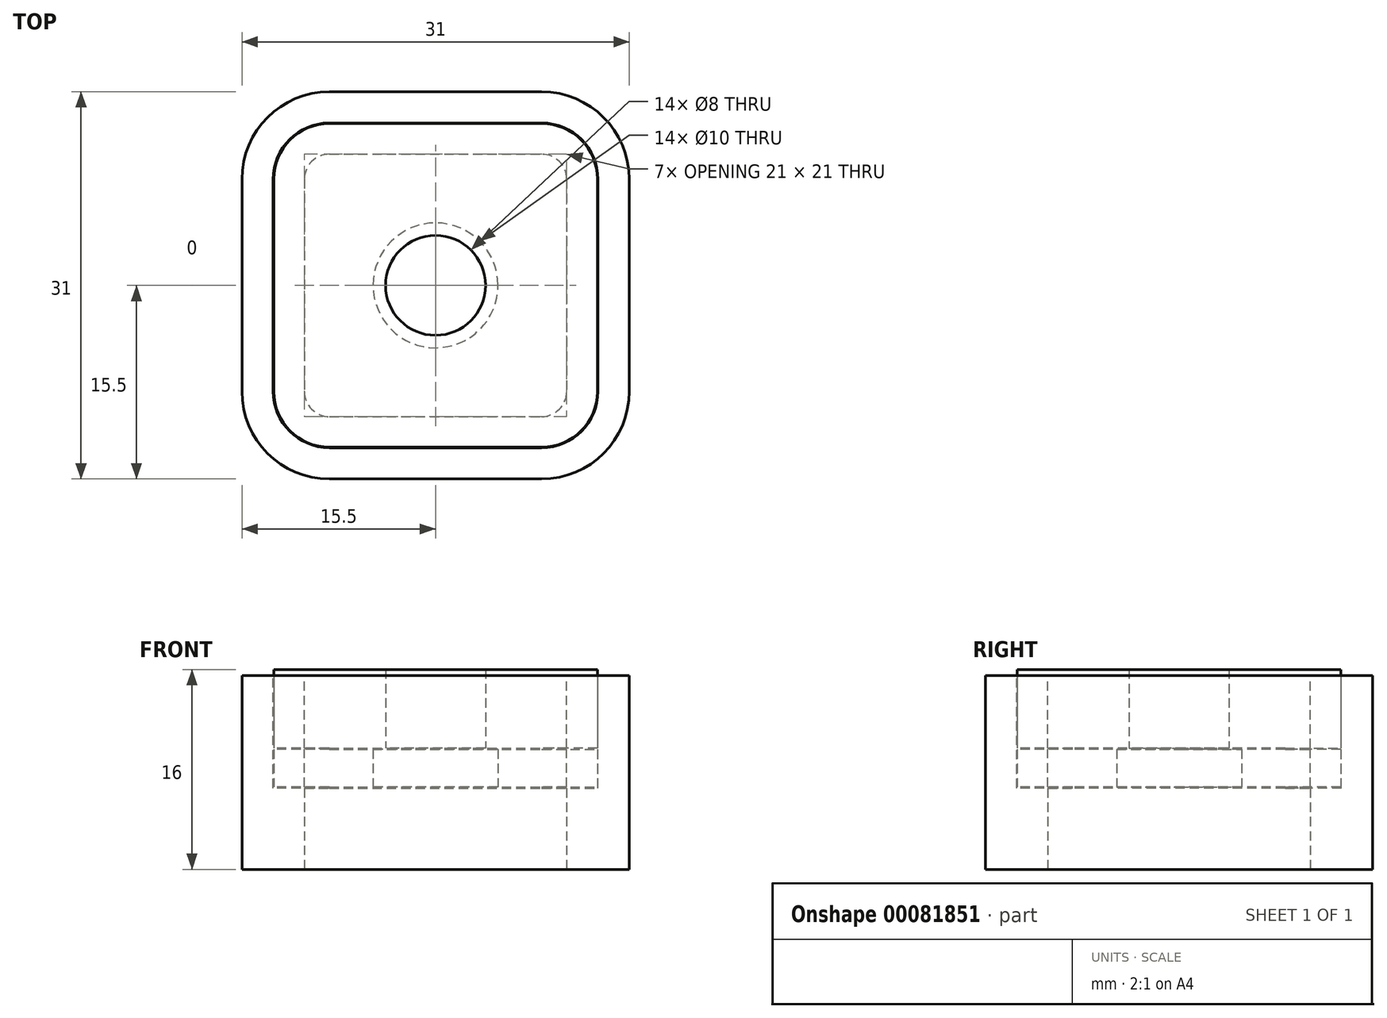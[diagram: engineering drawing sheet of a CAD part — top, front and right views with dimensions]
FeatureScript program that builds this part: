
annotation { "Feature Type Name" : "Feature", "Feature Type Description" : "" }
export const myFeature = defineFeature(function(context is Context, id is Id, definition is map)
    precondition{}
    {
        {
            var Q0;
            Q0=qCreatedBy(makeId("Top.planeOp"),FACE);
            var sketch = newSketch(context, id + "F0", { "sketchPlane" : qUnion([Q0])});
            skLineSegment(sketch, "E0.bottom", {"start": v(-8.5, 10.5) * mm, "end": v(8.5, 10.5) * mm});
            skLineSegment(sketch, "E0.top", {"start": v(-8.5, -10.5) * mm, "end": v(8.5, -10.5) * mm});
            skLineSegment(sketch, "E0.left", {"start": v(-10.5, 8.5) * mm, "end": v(-10.5, -8.5) * mm});
            skLineSegment(sketch, "E0.right", {"start": v(10.5, 8.5) * mm, "end": v(10.5, -8.5) * mm});
            skPoint(sketch, "E1.visualSharp", {"position": v(-10.5, 10.5) * mm});
            skArc(sketch, "E1.filletArc", {"start": v(-8.5, 10.5) * mm, "mid": v(-9.91, 9.91) * mm, "end": v(-10.5, 8.5) * mm});
            skPoint(sketch, "E2.visualSharp", {"position": v(10.5, 10.5) * mm});
            skArc(sketch, "E2.filletArc", {"start": v(10.5, 8.5) * mm, "mid": v(9.91, 9.91) * mm, "end": v(8.5, 10.5) * mm});
            skPoint(sketch, "E3.visualSharp", {"position": v(10.5, -10.5) * mm});
            skArc(sketch, "E3.filletArc", {"start": v(8.5, -10.5) * mm, "mid": v(9.91, -9.91) * mm, "end": v(10.5, -8.5) * mm});
            skPoint(sketch, "E4.visualSharp", {"position": v(-10.5, -10.5) * mm});
            skArc(sketch, "E4.filletArc", {"start": v(-10.5, -8.5) * mm, "mid": v(-9.91, -9.91) * mm, "end": v(-8.5, -10.5) * mm});
            skArc(sketch, "E5.0", {"start": v(-8.5, 15.5) * mm, "mid": v(-13.45, 13.45) * mm, "end": v(-15.5, 8.5) * mm});
            skLineSegment(sketch, "E5.1", {"start": v(-15.5, 8.5) * mm, "end": v(-15.5, -8.5) * mm});
            skLineSegment(sketch, "E5.2", {"start": v(-8.5, 15.5) * mm, "end": v(8.5, 15.5) * mm});
            skArc(sketch, "E5.3", {"start": v(-15.5, -8.5) * mm, "mid": v(-13.45, -13.45) * mm, "end": v(-8.5, -15.5) * mm});
            skArc(sketch, "E5.4", {"start": v(15.5, 8.5) * mm, "mid": v(13.45, 13.45) * mm, "end": v(8.5, 15.5) * mm});
            skLineSegment(sketch, "E5.5", {"start": v(15.5, 8.5) * mm, "end": v(15.5, -8.5) * mm});
            skArc(sketch, "E5.6", {"start": v(8.5, -15.5) * mm, "mid": v(13.45, -13.45) * mm, "end": v(15.5, -8.5) * mm});
            skLineSegment(sketch, "E5.7", {"start": v(-8.5, -15.5) * mm, "end": v(8.5, -15.5) * mm});
            skSolve(sketch);
        }
        {
            var Q0;
            Q0 = qSketchRegion(id + "F0", true);
            extrude(context, id + "F1", {"entities" : qUnion([Q0]), "depth" : 12.5 * mm});
        }
        {
            var Q0;
            Q0=makeQuery(id+"F1.opExtrude","CAP_FACE",FACE,{"disambiguationData":[OSD([sQuery(id+"F0.wireOp",EDGE,"E0.bottom"),sQuery(id+"F0.wireOp",EDGE,"E0.top"),sQuery(id+"F0.wireOp",EDGE,"E0.left"),sQuery(id+"F0.wireOp",EDGE,"E0.right"),sQuery(id+"F0.wireOp",EDGE,"E1.filletArc"),sQuery(id+"F0.wireOp",EDGE,"E2.filletArc"),sQuery(id+"F0.wireOp",EDGE,"E3.filletArc"),sQuery(id+"F0.wireOp",EDGE,"E4.filletArc"),sQuery(id+"F0.wireOp",EDGE,"E5.0"),sQuery(id+"F0.wireOp",EDGE,"E5.1"),sQuery(id+"F0.wireOp",EDGE,"E5.2"),sQuery(id+"F0.wireOp",EDGE,"E5.3"),sQuery(id+"F0.wireOp",EDGE,"E5.4"),sQuery(id+"F0.wireOp",EDGE,"E5.5"),sQuery(id+"F0.wireOp",EDGE,"E5.6"),sQuery(id+"F0.wireOp",EDGE,"E5.7")])],"isStart":false});
            var sketch = newSketch(context, id + "F2", { "sketchPlane" : qUnion([Q0])});
            skLineSegment(sketch, "E6.0", {"start": v(-8.5, 10.5) * mm, "end": v(8.5, 10.5) * mm});
            skArc(sketch, "E6.1", {"start": v(10.5, 8.5) * mm, "mid": v(9.91, 9.91) * mm, "end": v(8.5, 10.5) * mm});
            skLineSegment(sketch, "E6.2", {"start": v(10.5, 8.5) * mm, "end": v(10.5, -8.5) * mm});
            skArc(sketch, "E6.3", {"start": v(8.5, -10.5) * mm, "mid": v(9.91, -9.91) * mm, "end": v(10.5, -8.5) * mm});
            skLineSegment(sketch, "E6.4", {"start": v(-8.5, -10.5) * mm, "end": v(8.5, -10.5) * mm});
            skArc(sketch, "E6.5", {"start": v(-10.5, -8.5) * mm, "mid": v(-9.91, -9.91) * mm, "end": v(-8.5, -10.5) * mm});
            skLineSegment(sketch, "E6.6", {"start": v(-10.5, 8.5) * mm, "end": v(-10.5, -8.5) * mm});
            skArc(sketch, "E6.7", {"start": v(-8.5, 10.5) * mm, "mid": v(-9.91, 9.91) * mm, "end": v(-10.5, 8.5) * mm});
            skLineSegment(sketch, "E7.0", {"start": v(-8.5, 13) * mm, "end": v(8.5, 13) * mm});
            skArc(sketch, "E7.1", {"start": v(13, 8.5) * mm, "mid": v(11.68, 11.68) * mm, "end": v(8.5, 13) * mm});
            skArc(sketch, "E7.2", {"start": v(-8.5, 13) * mm, "mid": v(-11.68, 11.68) * mm, "end": v(-13, 8.5) * mm});
            skLineSegment(sketch, "E7.3", {"start": v(13, 8.5) * mm, "end": v(13, -8.5) * mm});
            skLineSegment(sketch, "E7.4", {"start": v(-13, 8.5) * mm, "end": v(-13, -8.5) * mm});
            skArc(sketch, "E7.5", {"start": v(-13, -8.5) * mm, "mid": v(-11.68, -11.68) * mm, "end": v(-8.5, -13) * mm});
            skLineSegment(sketch, "E7.6", {"start": v(-8.5, -13) * mm, "end": v(8.5, -13) * mm});
            skArc(sketch, "E7.7", {"start": v(8.5, -13) * mm, "mid": v(11.68, -11.68) * mm, "end": v(13, -8.5) * mm});
            skSolve(sketch);
        }
        {
            var Q0;
            Q0 = qSketchRegion(id + "F2", true);
            extrude(context, id + "F3", {"entities" : qUnion([Q0]), "operationType" : NewBodyOperationType.REMOVE, "oppositeDirection" : true, "depth" : 9 * mm});
        }
        {
            var Q0;
            Q0=makeQuery(id+"F3.boolean.opBoolean","COPY",FACE,{"derivedFrom":makeQuery(id+"F3.opExtrude","CAP_FACE",FACE,{"disambiguationData":[OSD([sQuery(id+"F2.wireOp",EDGE,"E6.0"),sQuery(id+"F2.wireOp",EDGE,"E6.1"),sQuery(id+"F2.wireOp",EDGE,"E6.2"),sQuery(id+"F2.wireOp",EDGE,"E6.3"),sQuery(id+"F2.wireOp",EDGE,"E6.4"),sQuery(id+"F2.wireOp",EDGE,"E6.5"),sQuery(id+"F2.wireOp",EDGE,"E6.6"),sQuery(id+"F2.wireOp",EDGE,"E6.7"),sQuery(id+"F2.wireOp",EDGE,"E7.0"),sQuery(id+"F2.wireOp",EDGE,"E7.1"),sQuery(id+"F2.wireOp",EDGE,"E7.2"),sQuery(id+"F2.wireOp",EDGE,"E7.3"),sQuery(id+"F2.wireOp",EDGE,"E7.4"),sQuery(id+"F2.wireOp",EDGE,"E7.5"),sQuery(id+"F2.wireOp",EDGE,"E7.6"),sQuery(id+"F2.wireOp",EDGE,"E7.7")])],"isStart":false})});
            cPlane(context, id + "F4", {"entities" : qUnion([Q0]), "cplaneType" : CPlaneType.OFFSET, "offset" : .1 * mm, "width" : 150 * mm, "height" : 150 * mm});
        }
        {
            var Q0;
            Q0=qCreatedBy(id+"F4.planeOp",FACE);
            var sketch = newSketch(context, id + "F5", { "sketchPlane" : qUnion([Q0])});
            skLineSegment(sketch, "E8.0", {"start": v(-8.5, 12.95) * mm, "end": v(8.5, 12.95) * mm});
            skArc(sketch, "E8.1", {"start": v(12.95, 8.5) * mm, "mid": v(11.65, 11.65) * mm, "end": v(8.5, 12.95) * mm});
            skArc(sketch, "E8.2", {"start": v(-8.5, 12.95) * mm, "mid": v(-11.65, 11.65) * mm, "end": v(-12.95, 8.5) * mm});
            skLineSegment(sketch, "E8.3", {"start": v(12.95, 8.5) * mm, "end": v(12.95, -8.5) * mm});
            skLineSegment(sketch, "E8.4", {"start": v(-12.95, 8.5) * mm, "end": v(-12.95, -8.5) * mm});
            skArc(sketch, "E8.5", {"start": v(-12.95, -8.5) * mm, "mid": v(-11.65, -11.65) * mm, "end": v(-8.5, -12.95) * mm});
            skLineSegment(sketch, "E8.6", {"start": v(-8.5, -12.95) * mm, "end": v(8.5, -12.95) * mm});
            skArc(sketch, "E8.7", {"start": v(8.5, -12.95) * mm, "mid": v(11.65, -11.65) * mm, "end": v(12.95, -8.5) * mm});
            skCircle(sketch, "E9", {"center": v(0, 0) * mm, "radius": 5 * mm});
            skSolve(sketch);
        }
        {
            var Q0;
            Q0 = qSketchRegion(id + "F5", true);
            extrude(context, id + "F6", {"entities" : qUnion([Q0]), "depth" : 3 * mm});
        }
        {
            var Q0;
            Q0=makeQuery(id+"F6.opExtrude","CAP_FACE",FACE,{"disambiguationData":[OSD([sQuery(id+"F5.wireOp",EDGE,"E8.0"),sQuery(id+"F5.wireOp",EDGE,"E8.1"),sQuery(id+"F5.wireOp",EDGE,"E8.2"),sQuery(id+"F5.wireOp",EDGE,"E8.3"),sQuery(id+"F5.wireOp",EDGE,"E8.4"),sQuery(id+"F5.wireOp",EDGE,"E8.5"),sQuery(id+"F5.wireOp",EDGE,"E8.6"),sQuery(id+"F5.wireOp",EDGE,"E8.7"),sQuery(id+"F5.wireOp",EDGE,"E9")])],"isStart":false});
            cPlane(context, id + "F7", {"entities" : qUnion([Q0]), "cplaneType" : CPlaneType.OFFSET, "offset" : .1 * mm, "width" : 150 * mm, "height" : 150 * mm});
        }
        {
            var Q0;
            Q0=qCreatedBy(id+"F7.planeOp",FACE);
            var sketch = newSketch(context, id + "F8", { "sketchPlane" : qUnion([Q0])});
            skLineSegment(sketch, "E10.0.0", {"start": v(8.5, 12.95) * mm, "end": v(-8.5, 12.95) * mm});
            skArc(sketch, "E10.0.1", {"start": v(-8.5, 12.95) * mm, "mid": v(-11.65, 11.65) * mm, "end": v(-12.95, 8.5) * mm});
            skLineSegment(sketch, "E10.0.2", {"start": v(-12.95, 8.5) * mm, "end": v(-12.95, -8.5) * mm});
            skArc(sketch, "E10.0.3", {"start": v(-12.95, -8.5) * mm, "mid": v(-11.65, -11.65) * mm, "end": v(-8.5, -12.95) * mm});
            skLineSegment(sketch, "E10.0.4", {"start": v(-8.5, -12.95) * mm, "end": v(8.5, -12.95) * mm});
            skArc(sketch, "E10.0.5", {"start": v(8.5, -12.95) * mm, "mid": v(11.65, -11.65) * mm, "end": v(12.95, -8.5) * mm});
            skLineSegment(sketch, "E10.0.6", {"start": v(12.95, -8.5) * mm, "end": v(12.95, 8.5) * mm});
            skArc(sketch, "E10.0.7", {"start": v(12.95, 8.5) * mm, "mid": v(11.65, 11.65) * mm, "end": v(8.5, 12.95) * mm});
            skCircle(sketch, "E11", {"center": v(0, 0) * mm, "radius": 4 * mm});
            skSolve(sketch);
        }
        {
            var Q0;
            Q0 = qSketchRegion(id + "F8", true);
            extrude(context, id + "F9", {"entities" : qUnion([Q0]), "depth" : 6.3 * mm});
        }
        {
            var Q0;
            Q0=makeQuery(id+"F1.opExtrude","CAP_FACE",FACE,{"disambiguationData":[OSD([sQuery(id+"F0.wireOp",EDGE,"E0.bottom"),sQuery(id+"F0.wireOp",EDGE,"E0.top"),sQuery(id+"F0.wireOp",EDGE,"E0.left"),sQuery(id+"F0.wireOp",EDGE,"E0.right"),sQuery(id+"F0.wireOp",EDGE,"E1.filletArc"),sQuery(id+"F0.wireOp",EDGE,"E2.filletArc"),sQuery(id+"F0.wireOp",EDGE,"E3.filletArc"),sQuery(id+"F0.wireOp",EDGE,"E4.filletArc"),sQuery(id+"F0.wireOp",EDGE,"E5.0"),sQuery(id+"F0.wireOp",EDGE,"E5.1"),sQuery(id+"F0.wireOp",EDGE,"E5.2"),sQuery(id+"F0.wireOp",EDGE,"E5.3"),sQuery(id+"F0.wireOp",EDGE,"E5.4"),sQuery(id+"F0.wireOp",EDGE,"E5.5"),sQuery(id+"F0.wireOp",EDGE,"E5.6"),sQuery(id+"F0.wireOp",EDGE,"E5.7")])],"isStart":true});
            var sketch = newSketch(context, id + "F10", { "sketchPlane" : qUnion([Q0])});
            skLineSegment(sketch, "E12.0.0", {"start": v(-8.5, -15.5) * mm, "end": v(8.5, -15.5) * mm});
            skArc(sketch, "E12.0.1", {"start": v(8.5, -15.5) * mm, "mid": v(13.45, -13.45) * mm, "end": v(15.5, -8.5) * mm});
            skLineSegment(sketch, "E12.0.2", {"start": v(15.5, -8.5) * mm, "end": v(15.5, 8.5) * mm});
            skArc(sketch, "E12.0.3", {"start": v(15.5, 8.5) * mm, "mid": v(13.45, 13.45) * mm, "end": v(8.5, 15.5) * mm});
            skLineSegment(sketch, "E12.0.4", {"start": v(8.5, 15.5) * mm, "end": v(-8.5, 15.5) * mm});
            skArc(sketch, "E12.0.5", {"start": v(-8.5, 15.5) * mm, "mid": v(-13.45, 13.45) * mm, "end": v(-15.5, 8.5) * mm});
            skLineSegment(sketch, "E12.0.6", {"start": v(-15.5, 8.5) * mm, "end": v(-15.5, -8.5) * mm});
            skArc(sketch, "E12.0.7", {"start": v(-15.5, -8.5) * mm, "mid": v(-13.45, -13.45) * mm, "end": v(-8.5, -15.5) * mm});
            skLineSegment(sketch, "E13.0", {"start": v(-8.5, 10.5) * mm, "end": v(8.5, 10.5) * mm});
            skArc(sketch, "E14.0", {"start": v(8.5, 10.5) * mm, "mid": v(9.91, 9.91) * mm, "end": v(10.5, 8.5) * mm});
            skLineSegment(sketch, "E15.0", {"start": v(10.5, -8.5) * mm, "end": v(10.5, 8.5) * mm});
            skArc(sketch, "E16.0", {"start": v(10.5, -8.5) * mm, "mid": v(9.91, -9.91) * mm, "end": v(8.5, -10.5) * mm});
            skLineSegment(sketch, "E17.0", {"start": v(-8.5, -10.5) * mm, "end": v(8.5, -10.5) * mm});
            skLineSegment(sketch, "E18.0", {"start": v(-10.5, -8.5) * mm, "end": v(-10.5, 8.5) * mm});
            skArc(sketch, "E19.0", {"start": v(-10.5, 8.5) * mm, "mid": v(-9.91, 9.91) * mm, "end": v(-8.5, 10.5) * mm});
            skArc(sketch, "E20.0", {"start": v(-8.5, -10.5) * mm, "mid": v(-9.91, -9.91) * mm, "end": v(-10.5, -8.5) * mm});
            skSolve(sketch);
        }
        {
            var Q0;
            Q0 = qSketchRegion(id + "F10", true);
            extrude(context, id + "F11", {"entities" : qUnion([Q0]), "operationType" : NewBodyOperationType.ADD, "depth" : 3 * mm});
        }
    });
